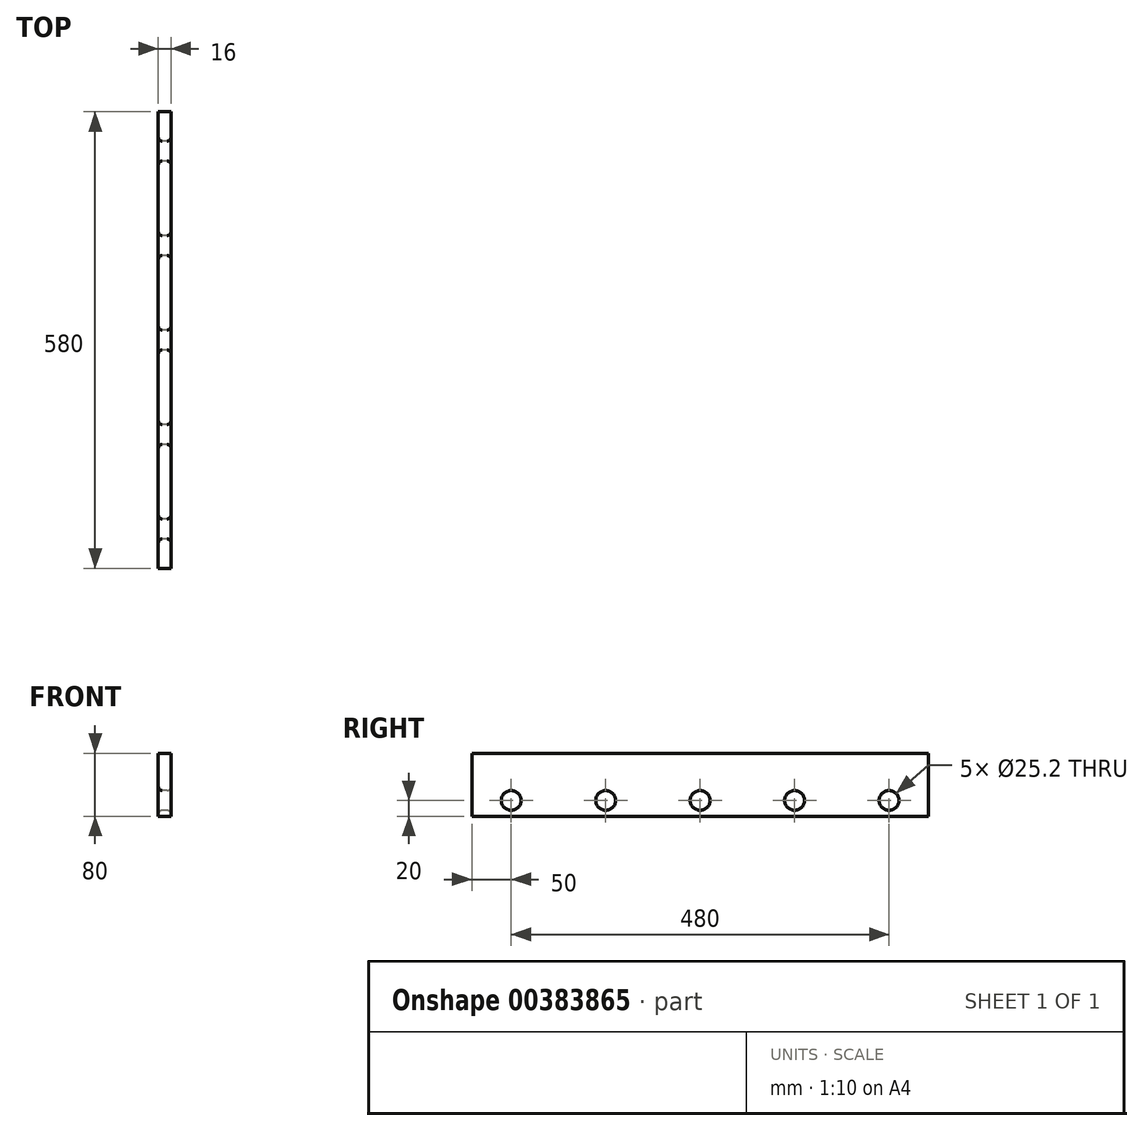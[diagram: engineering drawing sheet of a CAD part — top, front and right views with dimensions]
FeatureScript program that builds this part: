
annotation { "Feature Type Name" : "Feature", "Feature Type Description" : "" }
export const myFeature = defineFeature(function(context is Context, id is Id, definition is map)
    precondition{}
    {
        {
            var Q0;
            Q0=qCreatedBy(makeId("Right.planeOp"),FACE);
            var sketch = newSketch(context, id + "F0", { "sketchPlane" : qUnion([Q0])});
            skLineSegment(sketch, "E0.bottom", {"start": v(290, -40) * mm, "end": v(-290, -40) * mm});
            skLineSegment(sketch, "E0.top", {"start": v(290, 40) * mm, "end": v(-290, 40) * mm});
            skLineSegment(sketch, "E0.left", {"start": v(290, -40) * mm, "end": v(290, 40) * mm});
            skLineSegment(sketch, "E0.right", {"start": v(-290, -40) * mm, "end": v(-290, 40) * mm});
            skPoint(sketch, "E0.middle", {"position": v(0, 0) * mm});
            skLineSegment(sketch, "E1", {"start": v(-290, -20) * mm, "end": v(290, -20) * mm, "construction": true});
            skCircle(sketch, "E2", {"center": v(-240, -20) * mm, "radius": 12.6 * mm});
            skCircle(sketch, "E3", {"center": v(-120, -20) * mm, "radius": 12.6 * mm});
            skCircle(sketch, "E4", {"center": v(0, -20) * mm, "radius": 12.6 * mm});
            skCircle(sketch, "E5", {"center": v(120, -20) * mm, "radius": 12.6 * mm});
            skCircle(sketch, "E6", {"center": v(240, -20) * mm, "radius": 12.6 * mm});
            skSolve(sketch);
        }
        {
            var Q0;
            Q0 = qSketchRegion(id + "F0", true);
            extrude(context, id + "F1", {"entities" : qUnion([Q0]), "depth" : 16 * mm});
        }
        {
            var Q0;
            Q0=makeQuery(id+"F1.opExtrude","CAP_EDGE",EDGE,{"disambiguationData":[OSD([sQuery(id+"F0.wireOp",EDGE,"E3")])],"isStart":true});
            var Q1;
            Q1=makeQuery(id+"F1.opExtrude","SWEPT_FACE",FACE,{"disambiguationData":[OSD([sQuery(id+"F0.wireOp",EDGE,"E3")])]});
            var Q2;
            Q2=makeQuery(id+"F1.opExtrude","CAP_EDGE",EDGE,{"disambiguationData":[OSD([sQuery(id+"F0.wireOp",EDGE,"E2")])],"isStart":false});
            var Q3;
            Q3=makeQuery(id+"F1.opExtrude","SWEPT_FACE",FACE,{"disambiguationData":[OSD([sQuery(id+"F0.wireOp",EDGE,"E2")])]});
            var Q4;
            Q4=makeQuery(id+"F1.opExtrude","CAP_EDGE",EDGE,{"disambiguationData":[OSD([sQuery(id+"F0.wireOp",EDGE,"E4")])],"isStart":true});
            var Q5;
            Q5=makeQuery(id+"F1.opExtrude","CAP_EDGE",EDGE,{"disambiguationData":[OSD([sQuery(id+"F0.wireOp",EDGE,"E4")])],"isStart":false});
            var Q6;
            Q6=makeQuery(id+"F1.opExtrude","CAP_EDGE",EDGE,{"disambiguationData":[OSD([sQuery(id+"F0.wireOp",EDGE,"E5")])],"isStart":true});
            var Q7;
            Q7=makeQuery(id+"F1.opExtrude","CAP_EDGE",EDGE,{"disambiguationData":[OSD([sQuery(id+"F0.wireOp",EDGE,"E5")])],"isStart":false});
            var Q8;
            Q8=makeQuery(id+"F1.opExtrude","CAP_EDGE",EDGE,{"disambiguationData":[OSD([sQuery(id+"F0.wireOp",EDGE,"E6")])],"isStart":false});
            var Q9;
            Q9=makeQuery(id+"F1.opExtrude","CAP_EDGE",EDGE,{"disambiguationData":[OSD([sQuery(id+"F0.wireOp",EDGE,"E6")])],"isStart":true});
            fillet(context, id + "F2", {"entities" : qUnion([Q0, Q1, Q2, Q3, Q4, Q5, Q6, Q7, Q8, Q9]), "radius" : 5 * mm, "tangentPropagation" : true, "allowEdgeOverflow" : false});
        }
    });
